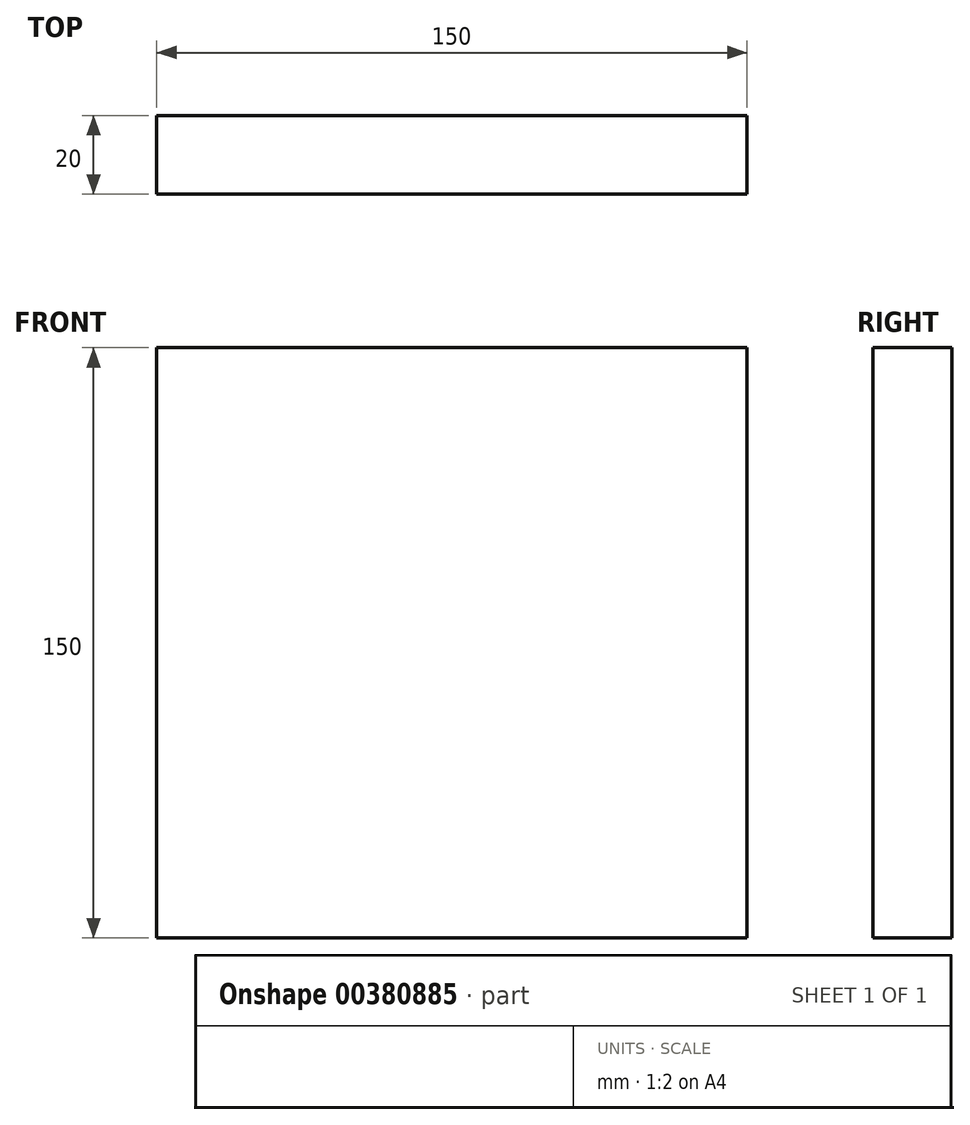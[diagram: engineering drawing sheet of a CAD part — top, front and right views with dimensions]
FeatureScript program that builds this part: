
annotation { "Feature Type Name" : "Feature", "Feature Type Description" : "" }
export const myFeature = defineFeature(function(context is Context, id is Id, definition is map)
    precondition{}
    {
        {
            var Q0;
            Q0=qCreatedBy(makeId("Front.planeOp"),FACE);
            var sketch = newSketch(context, id + "F0", { "sketchPlane" : qUnion([Q0])});
            skLineSegment(sketch, "E0.bottom", {"start": v(75, 75) * mm, "end": v(-75, 75) * mm});
            skLineSegment(sketch, "E0.top", {"start": v(75, -75) * mm, "end": v(-75, -75) * mm});
            skLineSegment(sketch, "E0.left", {"start": v(75, 75) * mm, "end": v(75, -75) * mm});
            skLineSegment(sketch, "E0.right", {"start": v(-75, 75) * mm, "end": v(-75, -75) * mm});
            skPoint(sketch, "E0.middle", {"position": v(0, 0) * mm});
            skSolve(sketch);
        }
        {
            var Q0;
            Q0 = qSketchRegion(id + "F0", true);
            extrude(context, id + "F1", {"entities" : qUnion([Q0]), "depth" : 20 * mm});
        }
    });
